# Revit family: Layout-Teknion-Zones_Digital_Lounge_Meeting_Four-R2022
name_source: partatom
category: Furniture Systems
units: mm (PartAtom-declared; Revit-internal decimal feet)

## family parameters
Always vertical = Yes
Cut with Voids When Loaded = No
OmniClass Number = 23.40.70.14.64.21
OmniClass Title = Systems Furniture
Part Type = Normal
Room Calculation Point = No
Round Connector Dimension = Use Diameter
Shared = No
Work Plane-Based = No

## types (1)
- Digital Lounge Meeting Zone Four
    Assembly Code = E2020200
    Default Elevation = 0"
    Description = 102" wide x 86" deep, 102" Diameter
    Manufacturer = Teknion
    Manufacturer Fax = 416.661.4586
    Model = Digital Lounge Meeting Zone - Four
    Part Number = ZNCAN
    Product Documentation Link = https://www.teknion.com
    Product Line = Zones
    Product Page URL = http://teknionplanningtool.com
    Sustainability Data = http://www.teknion.com
    URL = http://www.teknion.com
    Warranty = http://www.teknion.com

## geometry (parser evidence)
native form markers: Blend x28, Sweep x27
no freeform markers — native parametric forms only
